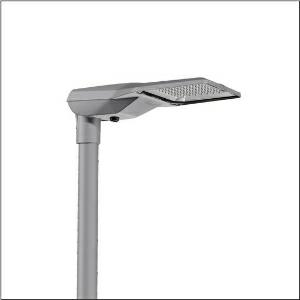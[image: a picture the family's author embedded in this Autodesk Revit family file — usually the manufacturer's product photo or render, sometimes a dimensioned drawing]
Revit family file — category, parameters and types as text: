
# Revit family: streetlight_sl_21_iq_midi___st1_0ab_5xe3m31u08nb_407f
name_source: partatom
category: Lighting Fixtures
units: mm (PartAtom-declared; Revit-internal decimal feet)

## family parameters
Cut with Voids When Loaded = No
Host = Face
Light Source = No
Part Type = Normal
Room Calculation Point = No
Round Connector Dimension = Use Diameter
Shared = No

## types (1)
- --- (1 x LED, 18970 lm, 136.6 W, 3000K)
    Apparent Load = 137 VA
    CIE Flux Codes = 40 74 97 100 100
    Color Rendering = 70
    Color Temperature = 3000K
    Default Elevation = 1800 mm
    Description = Streetlight SL 21 iQ midi, mast luminaire, primary light control with lens, of PMMA, primary optical cover: cover, of toughened safety glass, transparent, light distribution: ST1.0aB, light emission: direct distribution, primary light characteristic: asymmetric, installation type: post-top, side-entry, LED, High Power LED, rated luminous flux: 18.970lm, luminous efficacy: 139lm/W, light colour: 730, colour temperature: 3000K, control gear: iQ-Street Remote, D4i with power reduction, control: pre-setting: logarithmic dimming characteristic, Street-Remote, Auto-Match, Temp-Guard, Lumen-Switch, Night-Set, Smart-Wire, Light-Fading, Desk-Remote (wireless, voltage-free reading and setting of iQ features in the workshop via application-optimized NFC function/RFID function), optimised constant luminous flux control (CLO 2.0), mains connection: 230..240V, AC, 50/60Hz, start of lifetime: 137W, end of service life: 144W, reduction: 61W, luminaire housing, of diecast aluminium, powder-coated, Siteco® metallic grey (DB 702S), corrosivity category C5 mid according to DIN EN ISO 12944, please order mast flange separately, inclination adjustable: 0°, 5°, 10°, 15°, sealing non-destructively replaceable, multi-level sealing system, length: 644mm, width: 335mm, height: 110mm, mast flange for spigot size: 42mm (side-entry): 5XC10008XM4, 60/48mm (side-entry/post-top): 5XC10108XM2, 76/60mm (side-entry/post-top): 5XC10108XM1, mounting height: 4..8m, Smart Interface below, protection rating (complete): IP66, insulation class (complete): insulation class II (safety insulation), certification: CE, ENEC, ENEC+, VDE, impact resistance: IK10, permissible operating ambient temperature for outdoor applications: -40..+50°C, standard-compliant lighting for roads and squares, packaging unit: 1 piece

Light Distribution: ST1.0aB
    Height = 111 mm
    Lamp = 1 x LED
    Lamp Light Flux = 18970 lm
    Lamp Power = 136.6 W
    Lamp count = 1
    Length = 644 mm
    Luminous efficacy = 139 lm/W
    Manufacturer = Siteco
    ModVariant = No
    Model = 5XE3M31U08NB
    Number of Poles = 1
    OnlyDefault = Yes
    Power Factor = 1
    Product Name = Streetlight SL 21 iQ midi | ST1.0aB
    Product group = mast luminaire | pylon top
    ProductGroupID = 6100
    Protection Class = Protection class II
    Protection Degree = IP 66
    RLX_Detail_Level = 1
    RLX_Emergency_Light_Flux = 0 lm
    RLX_Emergency_Type = 0
    RLX_Emergency_Type_DB = No
    RlxData = <blob elided: 27237 chars, md5=86e80c72>
    Socket = socket
    Standby Power = 0 W
    System Light Flux = 18970 lm
    System Power = 137 W
    Type Comments = factory setting: luminous flux: 100 % | dim-lin: 254 | 733 mA
    Type Image = l_1004300.jpg
    URL = http://relux.com
    VarID = @adj_112134
    Voltage = 0 V
    Weight = 0.00 kg
    Width = 336 mm

## geometry (parser evidence)
native form markers: Blend x4, Sweep x10
no freeform markers — native parametric forms only
